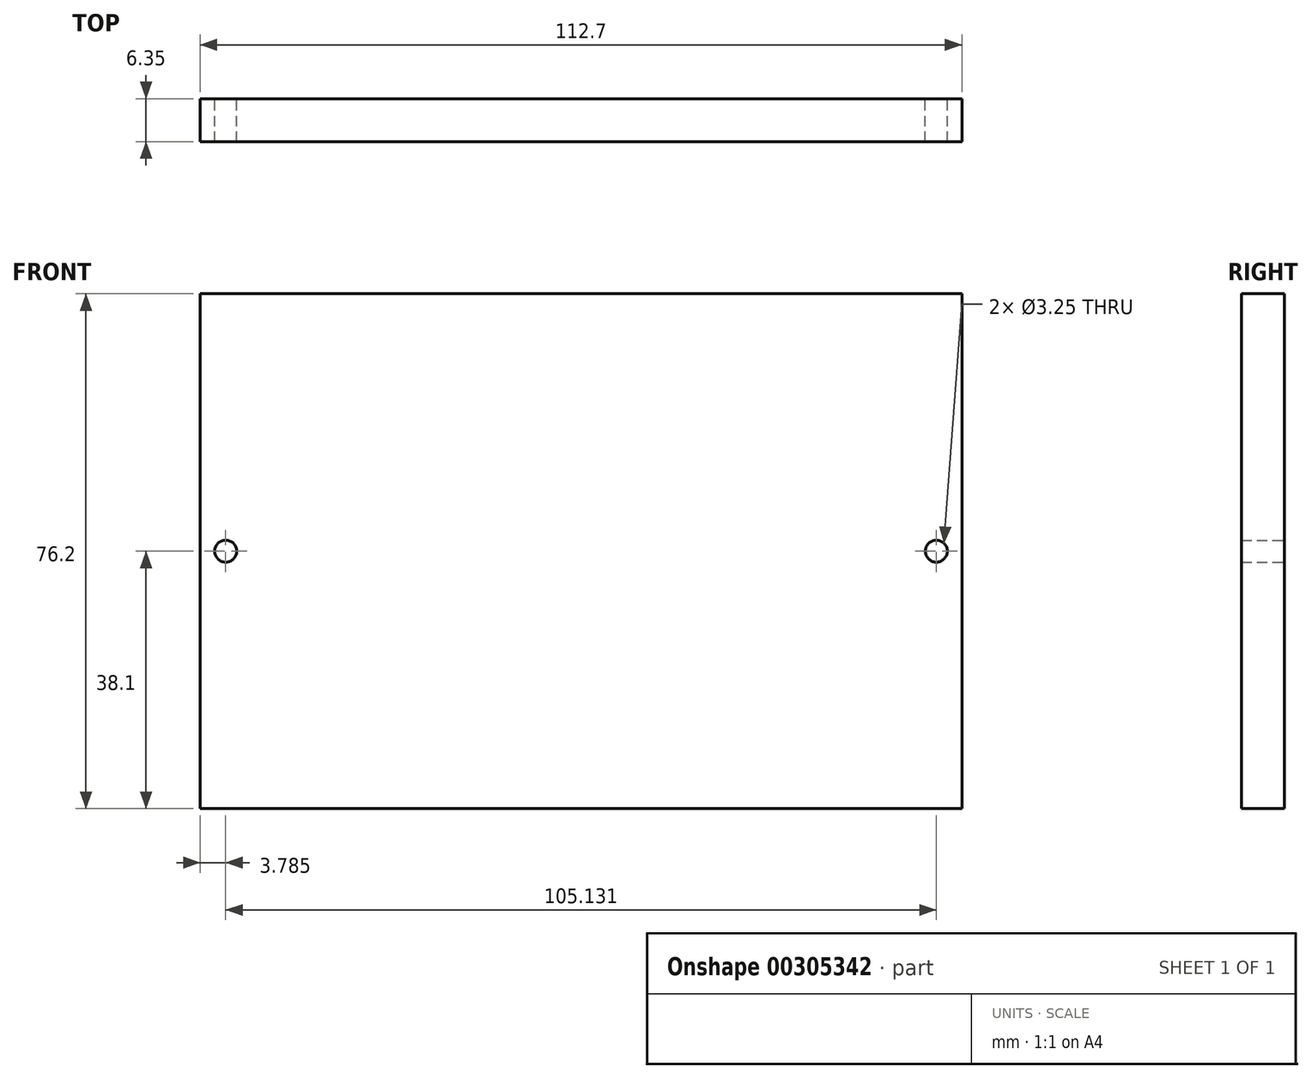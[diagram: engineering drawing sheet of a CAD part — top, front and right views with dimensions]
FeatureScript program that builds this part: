
annotation { "Feature Type Name" : "Feature", "Feature Type Description" : "" }
export const myFeature = defineFeature(function(context is Context, id is Id, definition is map)
    precondition{}
    {
        {
            var Q0;
            Q0=qCreatedBy(makeId("Front.planeOp"),FACE);
            var sketch = newSketch(context, id + "F0", { "sketchPlane" : qUnion([Q0])});
            skLineSegment(sketch, "E0.bottom", {"start": v(-56.35, 38.1) * mm, "end": v(56.35, 38.1) * mm});
            skLineSegment(sketch, "E0.top", {"start": v(-56.35, -38.1) * mm, "end": v(56.35, -38.1) * mm});
            skLineSegment(sketch, "E0.left", {"start": v(-56.35, 38.1) * mm, "end": v(-56.35, -38.1) * mm});
            skLineSegment(sketch, "E0.right", {"start": v(56.35, 38.1) * mm, "end": v(56.35, -38.1) * mm});
            skLineSegment(sketch, "E1", {"start": v(0, 0) * mm, "end": v(52.57, 0) * mm, "construction": true});
            skLineSegment(sketch, "E2", {"start": v(0, 0) * mm, "end": v(-52.57, 0) * mm, "construction": true});
            skCircle(sketch, "E3", {"center": v(-52.57, 0) * mm, "radius": 1.63 * mm});
            skCircle(sketch, "E4", {"center": v(52.57, 0) * mm, "radius": 1.63 * mm});
            skSolve(sketch);
        }
        {
            var Q0;
            Q0=makeQuery(id+"F0.imprint","IMPRINT",FACE,{"disambiguationData":[TD([[makeQuery(id+"F0.imprint","IMPRINT",EDGE,{"derivedFrom":sQuery(id+"F0.wireOp",EDGE,"E0.bottom")}),-1.0]])]});
            extrude(context, id + "F1", {"entities" : qUnion([Q0]), "depth" : 6.35 * mm});
        }
    });
